# Revit family: Hose-Stream-Rated_Smoke-Fire-Curtain_DoorSystems_DSI-HS10B-Multiple-Roller-Side-by-Side-Headbox
name_source: partatom
category: Doors
units: mm (PartAtom-declared; Revit-internal decimal feet)

## family parameters
Always vertical = Yes
Cut with Voids When Loaded = No
Host = Wall
OmniClass Number = 23.30.10.21.11.11
OmniClass Title = Rolling Fire Doors
Room Calculation Point = No
Shared = No

## types (3) — shared parameters
Analytic Construction = <None>
CAD Details = https://www.arcat.com
CurtainDrop_Viz = Yes
Define Thermal Properties by = Schematic Type
Description = Hose Stream Rated Smoke and Fire Curtain
Fire Performance = UL 10B
Fire Rating = 1, 2, 3
Frame Width = 0' - 4"
FrameDepth = 0' - 2"
HeadBox_Depth = 1' - 9"
HeadBox_Height = 1' - 0"
Invalid Model = No
Keynote = 08 33 44
Manufacturer = Door Systems
Model = DSI-HS10B
Product Page URL = https://www.arcat.com
Rough Height = 0' - 0"
Rough Width = 0' - 0"
Specification = https://www.arcat.com
URL = https://www.doorsysinc.com
Wall Closure = By host

## per-type parameters (varying)
| type | Auxiliary HeadBox_Depth | Auxiliary HeadBox_Height |
| 15" x 9" Head-box #1 | 1' - 3" | 0' - 9" |
| 18" x 10" Head-box #2 | 1' - 6" | 0' - 10" |
| 21" x 12" Head-box #3 | 1' - 9" | 1' - 0" |

## geometry (parser evidence)
native form markers: Sweep x2
no freeform markers — native parametric forms only
